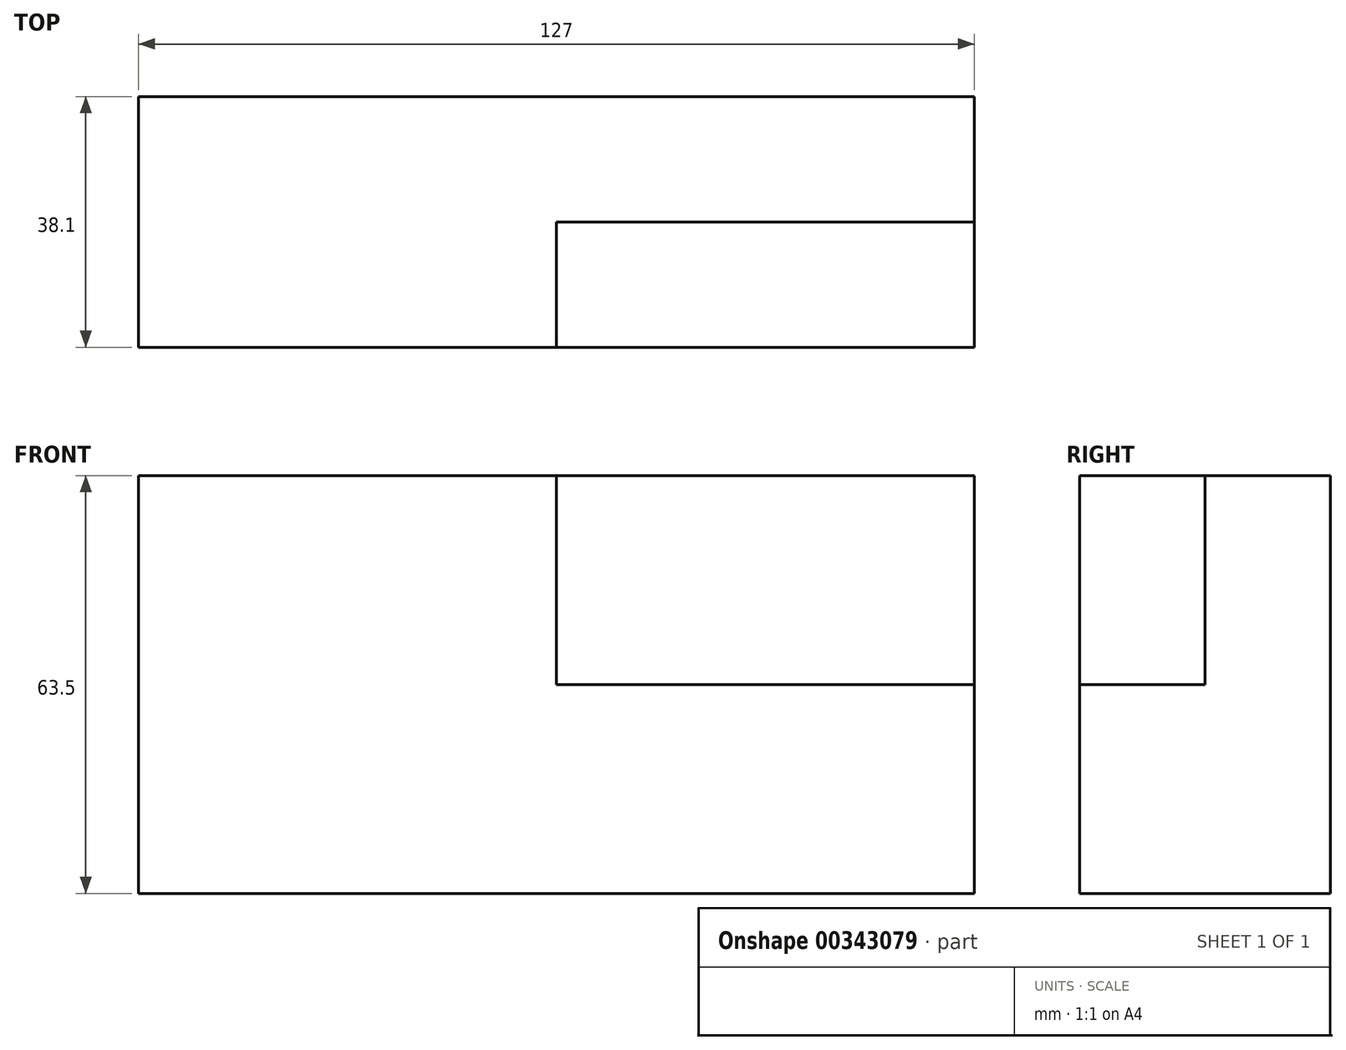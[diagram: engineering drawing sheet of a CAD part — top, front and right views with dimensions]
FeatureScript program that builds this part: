
annotation { "Feature Type Name" : "Feature", "Feature Type Description" : "" }
export const myFeature = defineFeature(function(context is Context, id is Id, definition is map)
    precondition{}
    {
        {
            var Q0;
            Q0=qCreatedBy(makeId("Front.planeOp"),FACE);
            var sketch = newSketch(context, id + "F0", { "sketchPlane" : qUnion([Q0])});
            skLineSegment(sketch, "E0", {"start": v(-67.16, -63.5) * mm, "end": v(59.84, -63.5) * mm});
            skLineSegment(sketch, "E1", {"start": v(-67.16, -63.5) * mm, "end": v(-67.16, 0) * mm});
            skLineSegment(sketch, "E2", {"start": v(-67.16, 0) * mm, "end": v(59.84, 0) * mm});
            skLineSegment(sketch, "E3", {"start": v(59.84, 0) * mm, "end": v(59.84, -63.5) * mm});
            skLineSegment(sketch, "E4", {"start": v(-3.66, -31.75) * mm, "end": v(59.84, -31.75) * mm});
            skLineSegment(sketch, "E5", {"start": v(-3.66, 0) * mm, "end": v(-3.66, -31.75) * mm});
            skSolve(sketch);
        }
        {
            var Q0;
            {var subQ4=sQuery(id+"F0.wireOp",EDGE,"E0");Q0=makeQuery(id+"F0.imprint","IMPRINT",FACE,{"disambiguationData":[TD([[makeQuery(id+"F0.imprint","IMPRINT",EDGE,{"derivedFrom":subQ4}),1.0]])]});}
            extrude(context, id + "F1", {"entities" : qUnion([Q0]), "depth" : 38.1 * mm});
        }
        {
            var Q0;
            Q0 = qSketchRegion(id + "F0", true);
            extrude(context, id + "F2", {"entities" : qUnion([Q0]), "operationType" : NewBodyOperationType.ADD, "depth" : 19.05 * mm});
        }
    });
